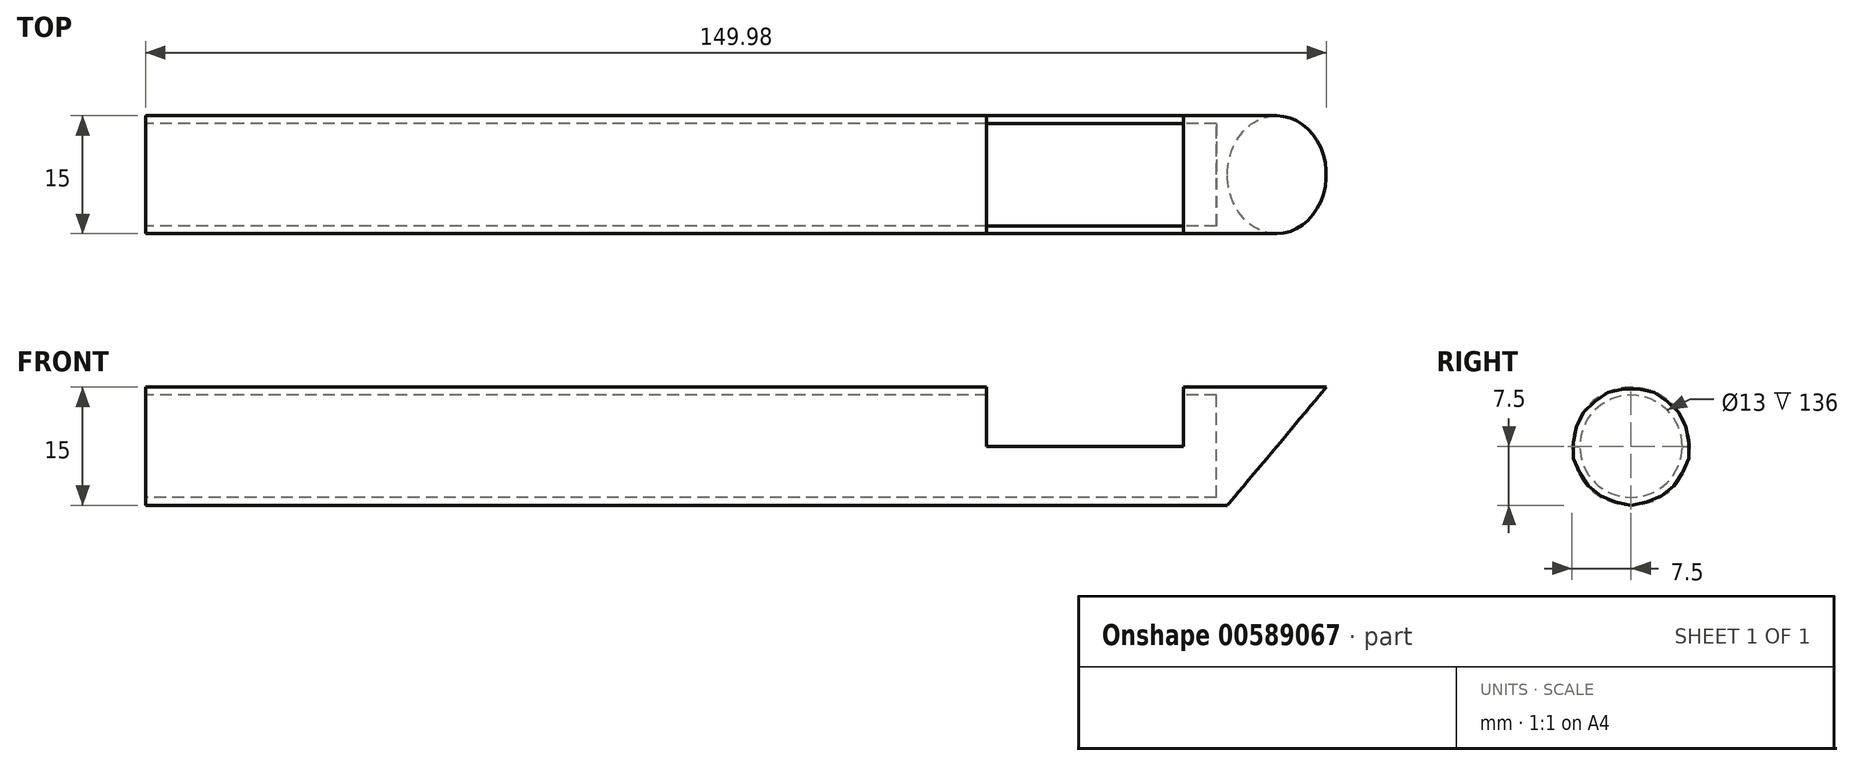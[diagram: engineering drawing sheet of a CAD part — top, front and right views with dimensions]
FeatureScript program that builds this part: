
annotation { "Feature Type Name" : "Feature", "Feature Type Description" : "" }
export const myFeature = defineFeature(function(context is Context, id is Id, definition is map)
    precondition{}
    {
        {
            var Q0;
            Q0=qCreatedBy(makeId("Right.planeOp"),FACE);
            var sketch = newSketch(context, id + "F0", { "sketchPlane" : qUnion([Q0])});
            skCircle(sketch, "E0", {"center": v(0, 0) * mm, "radius": 7.5 * mm});
            skSolve(sketch);
        }
        {
            var Q0;
            Q0 = qSketchRegion(id + "F0", true);
            extrude(context, id + "F1", {"entities" : qUnion([Q0]), "depth" : 150 * mm, "offsetDistance" : 25 * mm});
        }
        {
            var Q0;
            Q0=qCreatedBy(makeId("Front.planeOp"),FACE);
            var sketch = newSketch(context, id + "F2", { "sketchPlane" : qUnion([Q0])});
            skLineSegment(sketch, "E1", {"start": v(151.53, 9.35) * mm, "end": v(134.3, -11.2) * mm});
            skLineSegment(sketch, "E2", {"start": v(134.3, -11.2) * mm, "end": v(-5.4, -11.2) * mm});
            skLineSegment(sketch, "E3", {"start": v(-5.4, -11.2) * mm, "end": v(-5.4, 11.14) * mm});
            skLineSegment(sketch, "E4", {"start": v(-5.4, 11.14) * mm, "end": v(151.53, 9.35) * mm});
            skSolve(sketch);
        }
        {
            var Q0;
            Q0 = qSketchRegion(id + "F2", true);
            extrude(context, id + "F3", {"entities" : qUnion([Q0]), "operationType" : NewBodyOperationType.INTERSECT, "endBound" : BoundingType.SYMMETRIC, "depth" : 25 * mm, "offsetDistance" : 25 * mm});
        }
        {
            var Q0;
            Q0=qCreatedBy(makeId("Top.planeOp"),FACE);
            var sketch = newSketch(context, id + "F4", { "sketchPlane" : qUnion([Q0])});
            skLineSegment(sketch, "E5.bottom", {"start": v(131.83, -9.75) * mm, "end": v(106.83, -9.75) * mm});
            skLineSegment(sketch, "E5.top", {"start": v(131.83, 10.25) * mm, "end": v(106.83, 10.25) * mm});
            skLineSegment(sketch, "E5.left", {"start": v(131.83, -9.75) * mm, "end": v(131.83, 10.25) * mm});
            skLineSegment(sketch, "E5.right", {"start": v(106.83, -9.75) * mm, "end": v(106.83, 10.25) * mm});
            skSolve(sketch);
        }
        {
            var Q0;
            Q0 = qSketchRegion(id + "F4", true);
            extrude(context, id + "F5", {"entities" : qUnion([Q0]), "operationType" : NewBodyOperationType.REMOVE, "depth" : 36 * mm, "offsetDistance" : 25 * mm});
        }
        {
            var Q0;
            Q0=qCreatedBy(makeId("Right.planeOp"),FACE);
            var sketch = newSketch(context, id + "F6", { "sketchPlane" : qUnion([Q0])});
            skCircle(sketch, "E6", {"center": v(0, 0) * mm, "radius": 6.5 * mm});
            skSolve(sketch);
        }
        {
            var Q0;
            Q0 = qSketchRegion(id + "F6", true);
            extrude(context, id + "F7", {"entities" : qUnion([Q0]), "operationType" : NewBodyOperationType.REMOVE, "depth" : 136 * mm, "offsetDistance" : 25 * mm});
        }
    });
